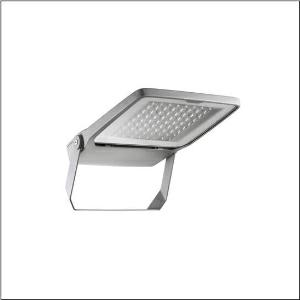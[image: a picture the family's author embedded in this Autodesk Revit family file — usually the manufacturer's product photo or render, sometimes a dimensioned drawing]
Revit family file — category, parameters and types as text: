
# Revit family: floodlight_fl_20_mini___pl61_5xa7671b2c1ac_3475
name_source: partatom
category: Lighting Fixtures
units: mm (PartAtom-declared; Revit-internal decimal feet)

## family parameters
Cut with Voids When Loaded = No
Host = Face
Light Source = No
Part Type = Normal
Room Calculation Point = No
Round Connector Dimension = Use Diameter
Shared = No

## types (1)
- Floodlight FL 20 mini  PL61 (1 x LED 4000K / CRI = 70 (unbekannt), 6350 lm, 4000K)
    Apparent Load = 51 VA
    CIE Flux Codes = 33 65 98 100 100
    Color Rendering = 70
    Color Temperature = 4000K
    Default Elevation = 1800 mm
    Description = Floodlight FL 20 mini, floodlight, primary light control with lens, of plastic, primary optical cover: protective disc, of toughened safety glass, transparent, light distribution: PL61, light emission: direct distribution, primary light characteristic: asymmetric, installation type: surface-mounted, LED, High Power LED, rated luminous flux: 6.350lm, luminous efficacy: 125lm/W, light colour: 740, colour temperature: 4000K, control gear: ECG Basic, control: power reduction, overheat protection, electronic power reduction, with terminal, 5-pole, max. 2.5mm², mains connection: 220..240V, AC, 50/60Hz, rated input power: 51W, LED unit, of diecast aluminium, powder-coated, Siteco® metallic grey (DB 702S), corrosivity category C5 mid according to DIN EN ISO 12944, incl. 1x M20 cable gland for cable Ø 6.5..12mm, length: 446mm, width: 355mm, height: 62mm, housing frame, of diecast aluminium, powder-coated, Siteco® metallic grey (DB 702S), mounting bracket, of steel, powder-coated, Siteco® metallic grey (DB 702S), ON/OFF, protection rating (complete): IP66, insulation class (complete): insulation class I (protective earthing), certification: CE, ENEC, VDE, protection symbol: D, permissible operating ambient temperature: -40..+40°C, permissible operating ambient temperature for outdoor applications: -40..+50°C, standard: DIN EN 12944, packaging unit: 1 piece

Light Distribution: PL61
    Height = 62 mm  [stored 0.203412 ft]
    Lamp = 1 x LED 4000K / CRI >= 70 (unbekannt)
    Lamp Light Flux = 6350 lm
    Lamp count = 1
    Length = 467 mm
    Luminous efficacy = 125 lm/W
    Manufacturer = Siteco
    ModVariant = No
    Model = 5XA7671B2C1AC
    Mounting Place = Wall
    Mounting Type = Surface mounted
    Number of Poles = 1
    OnlyDefault = Yes
    Power Factor = 1
    Product Name = Floodlight FL 20 mini | PL61
    Product group = floodlight | wall mounted
    ProductGroupID = 2001
    Protection Class = Protection class I
    Protection Degree = IP 66
    RLX_Detail_Level = 1
    RLX_Emergency_Light_Flux = 0 lm
    RLX_Emergency_Type = 0
    RLX_Emergency_Type_DB = No
    RlxData = <blob elided: 71137 chars, md5=707fc7ac>
    Socket = socket
    Standby Power = 0 W
    System Light Flux = 6350 lm
    System Power = 51 W
    Type Comments = Product without accessories
    Type Image = l_1005948.jpg
    URL = http://relux.com
    VarID = ---
    Voltage = 0 V
    Weight = 0.00 kg
    Width = 335 mm

note: [stored X ft] marks values corroborated as IEEE doubles in the binary element streams (Revit-internal decimal feet)

## geometry (parser evidence)
native form markers: Blend x4, Sweep x12
no freeform markers — native parametric forms only
